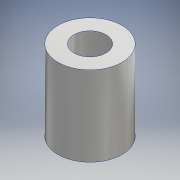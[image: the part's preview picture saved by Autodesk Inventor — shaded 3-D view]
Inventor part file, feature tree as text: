
AUTODESK INVENTOR PART (.ipt)
format: ipt  version: 2016 (Build 200138000, 138)  size: 96,768 bytes
history: native  units: mm
features: other x1, extrude x1, sketch x1
ambient origin geometry x8: Origin, YZ Plane, XZ Plane, XY Plane, X Axis, Y Axis, Z Axis, Center Point
bodies: Body1 (feature_tree)
feature tree (3):
  other  "ソリッド1"
  extrude  "押し出し1"  Depth=6.0mm
  sketch  "スケッチ1"
